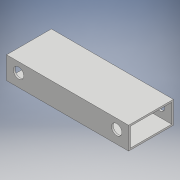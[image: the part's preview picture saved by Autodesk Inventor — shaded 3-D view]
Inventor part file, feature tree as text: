
AUTODESK INVENTOR PART (.ipt)
format: ipt  version: 2018 (Build 220112000, 112)  size: 111,616 bytes
history: native  units: mm
features: sketch x2, other x1, extrude x1, hole x1
ambient origin geometry x8: Origin, YZ Plane, XZ Plane, XY Plane, X Axis, Y Axis, Z Axis, Center Point
bodies: Body1 (feature_tree)
feature tree (5):
  other  "ソリッド1"
  extrude  "押し出し1"  Depth=60.0mm
  hole  "穴1"  [1 undecoded]
  sketch  "スケッチ1"
  sketch  "スケッチ2"
note: 1 required parameter value undecoded (feature->parameter linkage not recoverable at this tier; creation-order binding heuristic only, values carry confidence <= 0.55)
